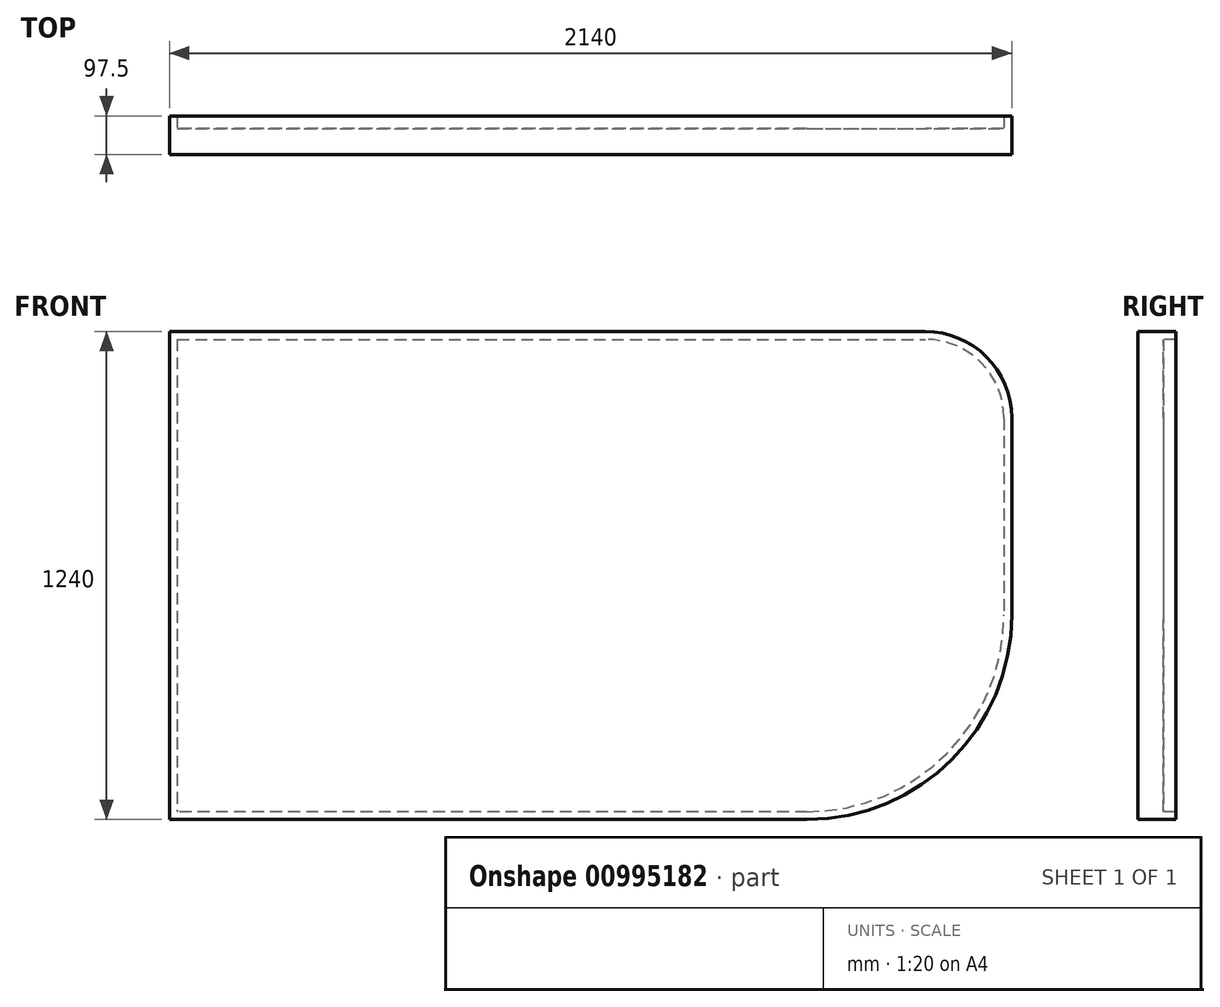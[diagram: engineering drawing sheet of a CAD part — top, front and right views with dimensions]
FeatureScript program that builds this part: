
annotation { "Feature Type Name" : "Feature", "Feature Type Description" : "" }
export const myFeature = defineFeature(function(context is Context, id is Id, definition is map)
    precondition{}
    {
        {
            var Q0;
            Q0=qCreatedBy(makeId("Front.planeOp"),FACE);
            var sketch = newSketch(context, id + "F0", { "sketchPlane" : qUnion([Q0])});
            skLineSegment(sketch, "E0", {"start": v(0, 0) * mm, "end": v(0, -1200) * mm});
            skLineSegment(sketch, "E1", {"start": v(0, 0) * mm, "end": v(1900, 0) * mm});
            skLineSegment(sketch, "E2", {"start": v(2100, -200) * mm, "end": v(2100, -700) * mm});
            skLineSegment(sketch, "E3", {"start": v(1600, -1200) * mm, "end": v(0, -1200) * mm});
            skPoint(sketch, "E4.visualSharp", {"position": v(2100, 0) * mm});
            skArc(sketch, "E4.filletArc", {"start": v(2100, -200) * mm, "mid": v(2041.42, -58.58) * mm, "end": v(1900, 0) * mm});
            skPoint(sketch, "E5.visualSharp", {"position": v(2100, -1200) * mm});
            skArc(sketch, "E5.filletArc", {"start": v(1600, -1200) * mm, "mid": v(1953.55, -1053.55) * mm, "end": v(2100, -700) * mm});
            skArc(sketch, "E6.0", {"start": v(1600, -1220) * mm, "mid": v(1967.7, -1067.7) * mm, "end": v(2120, -700) * mm});
            skLineSegment(sketch, "E6.1", {"start": v(-20, 20) * mm, "end": v(-20, -1220) * mm});
            skLineSegment(sketch, "E6.2", {"start": v(-20, 20) * mm, "end": v(1900, 20) * mm});
            skLineSegment(sketch, "E6.3", {"start": v(1600, -1220) * mm, "end": v(-20, -1220) * mm});
            skArc(sketch, "E6.4", {"start": v(2120, -200) * mm, "mid": v(2055.56, -44.44) * mm, "end": v(1900, 20) * mm});
            skLineSegment(sketch, "E6.5", {"start": v(2120, -200) * mm, "end": v(2120, -700) * mm});
            skSolve(sketch);
        }
        {
            var Q0;
            {var subQ0=sQuery(id+"F0.wireOp",EDGE,"7bd71d9f-be97-4365-bce9-49a19b9a43c3");var subQ1=makeQuery(id+"F0.imprint","INTERSECT",VERTEX,{"derivedFrom":[sQuery(id+"F0.wireOp",EDGE,"FreCxU7m-vOII-tjxF-Mfmg-pXKMQKg4E8Sy"),subQ0]});Q0=makeQuery(id+"F0.imprint","IMPRINT",FACE,{"disambiguationData":[TD([[makeQuery(id+"F0.imprint","IMPRINT",EDGE,{"disambiguationData":[TD([[subQ1,1.0]])],"derivedFrom":subQ0}),1.0]])]});}
            var Q1;
            Q1=makeQuery(id+"F0.imprint","IMPRINT",FACE,{"disambiguationData":[TD([[makeQuery(id+"F0.imprint","IMPRINT",EDGE,{"derivedFrom":sQuery(id+"F0.wireOp",EDGE,"E0")}),1.0]])]});
            extrude(context, id + "F1", {"entities" : qUnion([Q0, Q1]), "depth" : 65 * mm, "offsetDistance" : 25 * mm, "symmetric" : true});
        }
        {
            var Q0;
            Q0=makeQuery(id+"F0.imprint","IMPRINT",FACE,{"disambiguationData":[TD([[makeQuery(id+"F0.imprint","IMPRINT",EDGE,{"derivedFrom":sQuery(id+"F0.wireOp",EDGE,"E0")}),-1.0]])]});
            extrude(context, id + "F2", {"entities" : qUnion([Q0]), "operationType" : NewBodyOperationType.ADD, "depth" : -65 * mm, "offsetDistance" : 25 * mm});
        }
        {
            var Q0;
            Q0=makeQuery(id+"F0.imprint","IMPRINT",FACE,{"disambiguationData":[TD([[makeQuery(id+"F0.imprint","IMPRINT",EDGE,{"derivedFrom":sQuery(id+"F0.wireOp",EDGE,"E0")}),-1.0]])]});
            extrude(context, id + "F3", {"entities" : qUnion([Q0]), "operationType" : NewBodyOperationType.ADD, "depth" : 32.5 * mm, "offsetDistance" : 25 * mm});
        }
    });
